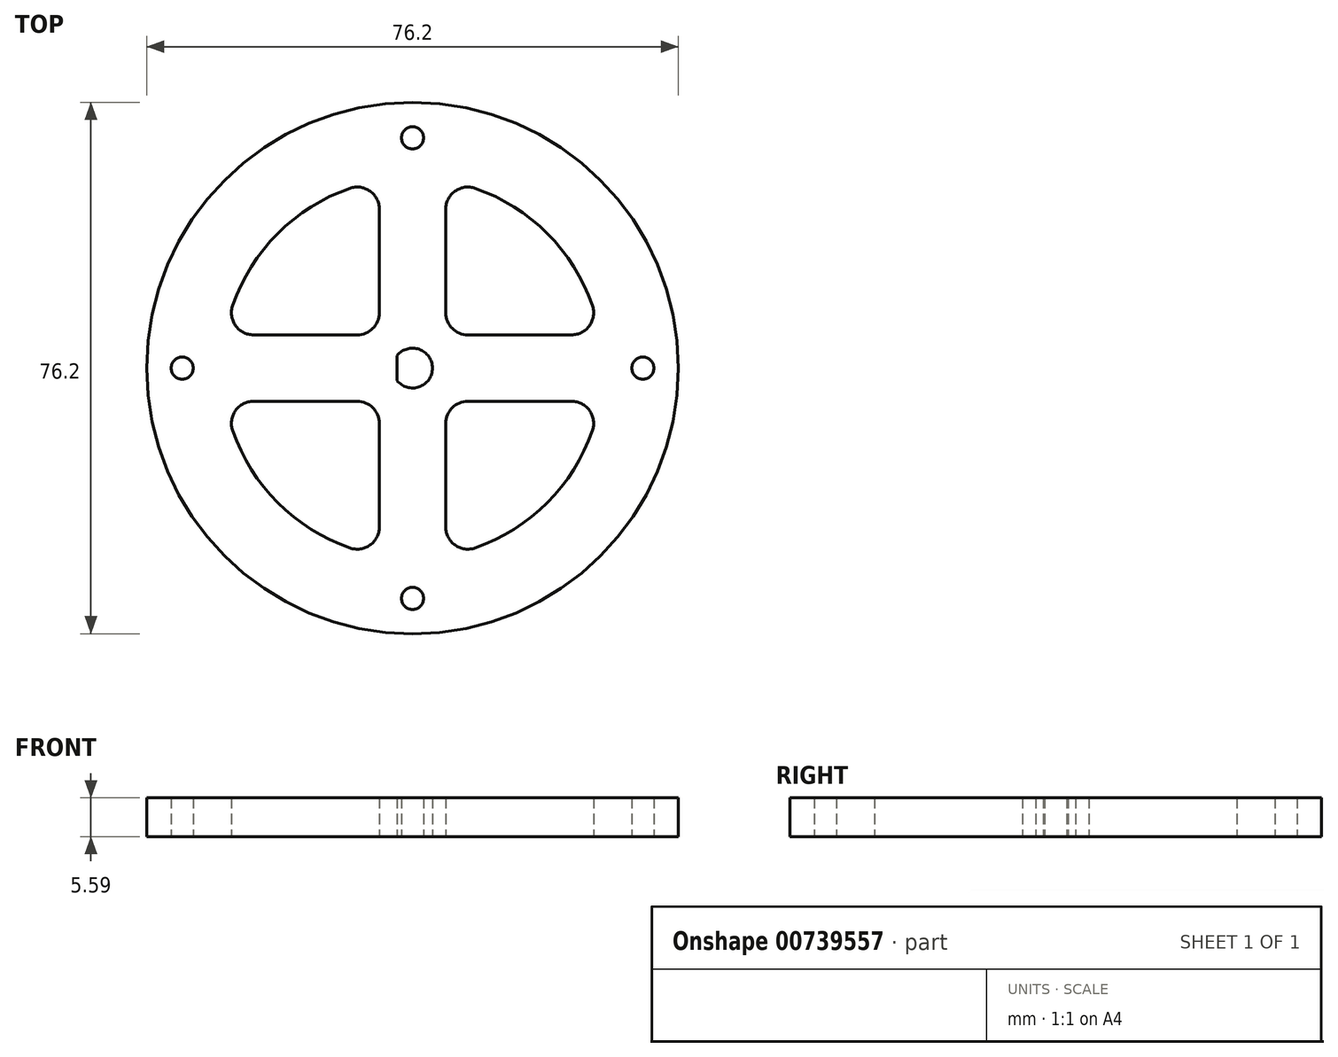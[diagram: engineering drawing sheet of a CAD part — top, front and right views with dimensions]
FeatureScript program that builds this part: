
annotation { "Feature Type Name" : "Feature", "Feature Type Description" : "" }
export const myFeature = defineFeature(function(context is Context, id is Id, definition is map)
    precondition{}
    {
        {
            var Q0;
            Q0=qCreatedBy(makeId("Top.planeOp"),FACE);
            var sketch = newSketch(context, id + "F0", { "sketchPlane" : qUnion([Q0])});
            skCircle(sketch, "E0", {"center": v(0, 0) * mm, "radius": 38.1 * mm});
            skArc(sketch, "E1", {"start": v(-2.22, -1.8) * mm, "mid": v(2.86, 0) * mm, "end": v(-2.22, 1.8) * mm});
            skLineSegment(sketch, "E2", {"start": v(-2.22, 1.8) * mm, "end": v(-2.22, -1.8) * mm});
            skCircle(sketch, "E3", {"center": v(0, 0) * mm, "radius": 33.02 * mm, "construction": true});
            skCircle(sketch, "E4", {"center": v(-33.02, 0) * mm, "radius": 1.59 * mm});
            skCircle(sketch, "E5", {"center": v(0, 33.02) * mm, "radius": 1.59 * mm});
            skCircle(sketch, "E6", {"center": v(33.02, 0) * mm, "radius": 1.59 * mm});
            skCircle(sketch, "E7", {"center": v(0, -33.02) * mm, "radius": 1.59 * mm});
            skSolve(sketch);
        }
        {
            var Q0;
            Q0=makeQuery(id+"F0.imprint","IMPRINT",FACE,{"disambiguationData":[TD([[makeQuery(id+"F0.imprint","IMPRINT",EDGE,{"derivedFrom":sQuery(id+"F0.wireOp",EDGE,"E0")}),1.0]])]});
            extrude(context, id + "F1", {"entities" : qUnion([Q0]), "depth" : 5.6 * mm, "offsetDistance" : 25.4 * mm});
        }
        {
            var Q0;
            Q0=qCreatedBy(makeId("Top.planeOp"),FACE);
            var sketch = newSketch(context, id + "F2", { "sketchPlane" : qUnion([Q0])});
            skLineSegment(sketch, "E8", {"start": v(7.94, 4.76) * mm, "end": v(22.79, 4.76) * mm});
            skLineSegment(sketch, "E9", {"start": v(4.76, 22.79) * mm, "end": v(4.76, 7.94) * mm});
            skArc(sketch, "E10", {"start": v(-8.98, 25.79) * mm, "mid": v(-19.3, 19.3) * mm, "end": v(-25.79, 8.98) * mm});
            skLineSegment(sketch, "E11.1.0", {"start": v(-22.79, 4.76) * mm, "end": v(-7.94, 4.76) * mm});
            skLineSegment(sketch, "E11.1.1", {"start": v(-4.76, 7.94) * mm, "end": v(-4.76, 22.79) * mm});
            skLineSegment(sketch, "E11.2.0", {"start": v(-4.76, -22.79) * mm, "end": v(-4.76, -7.94) * mm});
            skLineSegment(sketch, "E11.2.1", {"start": v(-7.94, -4.76) * mm, "end": v(-22.79, -4.76) * mm});
            skLineSegment(sketch, "E11.3.0", {"start": v(22.79, -4.76) * mm, "end": v(7.94, -4.76) * mm});
            skLineSegment(sketch, "E11.3.1", {"start": v(4.76, -7.94) * mm, "end": v(4.76, -22.79) * mm});
            skArc(sketch, "E12.trimOffspring", {"start": v(8.98, -25.79) * mm, "mid": v(19.3, -19.3) * mm, "end": v(25.79, -8.98) * mm});
            skArc(sketch, "E13.trimOffspring", {"start": v(-25.79, -8.98) * mm, "mid": v(-19.3, -19.3) * mm, "end": v(-8.98, -25.79) * mm});
            skArc(sketch, "E14.trimOffspring", {"start": v(25.79, 8.98) * mm, "mid": v(19.3, 19.3) * mm, "end": v(8.98, 25.79) * mm});
            skPoint(sketch, "E15.visualSharp", {"position": v(-4.76, 26.89) * mm});
            skArc(sketch, "E15.filletArc", {"start": v(-4.76, 22.79) * mm, "mid": v(-6.1, 25.38) * mm, "end": v(-8.98, 25.79) * mm});
            skPoint(sketch, "E16.visualSharp", {"position": v(-4.76, 4.76) * mm});
            skArc(sketch, "E16.filletArc", {"start": v(-7.94, 4.76) * mm, "mid": v(-5.7, 5.7) * mm, "end": v(-4.76, 7.94) * mm});
            skPoint(sketch, "E17.visualSharp", {"position": v(-26.89, 4.76) * mm});
            skArc(sketch, "E17.filletArc", {"start": v(-25.79, 8.98) * mm, "mid": v(-25.38, 6.1) * mm, "end": v(-22.79, 4.76) * mm});
            skPoint(sketch, "E18.visualSharp", {"position": v(-26.89, -4.76) * mm});
            skArc(sketch, "E18.filletArc", {"start": v(-22.79, -4.76) * mm, "mid": v(-25.38, -6.1) * mm, "end": v(-25.79, -8.98) * mm});
            skPoint(sketch, "E19.visualSharp", {"position": v(-4.76, -4.76) * mm});
            skArc(sketch, "E19.filletArc", {"start": v(-4.76, -7.94) * mm, "mid": v(-5.7, -5.7) * mm, "end": v(-7.94, -4.76) * mm});
            skPoint(sketch, "E20.visualSharp", {"position": v(-4.76, -26.89) * mm});
            skArc(sketch, "E20.filletArc", {"start": v(-8.98, -25.79) * mm, "mid": v(-6.1, -25.38) * mm, "end": v(-4.76, -22.79) * mm});
            skPoint(sketch, "E21.visualSharp", {"position": v(26.89, -4.76) * mm});
            skArc(sketch, "E21.filletArc", {"start": v(25.79, -8.98) * mm, "mid": v(25.38, -6.1) * mm, "end": v(22.79, -4.76) * mm});
            skPoint(sketch, "E22.visualSharp", {"position": v(4.76, -4.76) * mm});
            skArc(sketch, "E22.filletArc", {"start": v(7.94, -4.76) * mm, "mid": v(5.7, -5.7) * mm, "end": v(4.76, -7.94) * mm});
            skPoint(sketch, "E23.visualSharp", {"position": v(4.76, -26.89) * mm});
            skArc(sketch, "E23.filletArc", {"start": v(4.76, -22.79) * mm, "mid": v(6.1, -25.38) * mm, "end": v(8.98, -25.79) * mm});
            skPoint(sketch, "E24.visualSharp", {"position": v(26.89, 4.76) * mm});
            skArc(sketch, "E24.filletArc", {"start": v(22.79, 4.76) * mm, "mid": v(25.38, 6.1) * mm, "end": v(25.79, 8.98) * mm});
            skPoint(sketch, "E25.visualSharp", {"position": v(4.76, 26.89) * mm});
            skArc(sketch, "E25.filletArc", {"start": v(8.98, 25.79) * mm, "mid": v(6.1, 25.38) * mm, "end": v(4.76, 22.79) * mm});
            skPoint(sketch, "E26.visualSharp", {"position": v(4.76, 4.76) * mm});
            skArc(sketch, "E26.filletArc", {"start": v(4.76, 7.94) * mm, "mid": v(5.7, 5.7) * mm, "end": v(7.94, 4.76) * mm});
            skSolve(sketch);
        }
        {
            var Q0;
            Q0 = qSketchRegion(id + "F2", true);
            extrude(context, id + "F3", {"entities" : qUnion([Q0]), "operationType" : NewBodyOperationType.REMOVE, "endBound" : BoundingType.THROUGH_ALL, "depth" : 25.4 * mm, "offsetDistance" : 25.4 * mm});
        }
    });
